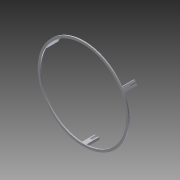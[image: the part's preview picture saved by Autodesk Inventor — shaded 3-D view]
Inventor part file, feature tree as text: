
AUTODESK INVENTOR PART (.ipt)
format: ipt  version: 2014 (Build 180170000, 170)  size: 248,832 bytes
history: native  units: mm
features: extrude x5, sketch x5
ambient origin geometry x8: Origin, YZ Plane, XZ Plane, XY Plane, X Axis, Y Axis, Z Axis, Center Point
bodies: Solid1 (feature_tree)
feature tree (10):
  extrude  "Extrusion1"  Depth=75.0mm
  extrude  "Extrusion2"  Depth=1.0mm
  extrude  "Extrusion3"  Depth=0.74mm
  extrude  "Extrusion4"  TaperAngle=45.0deg  [1 undecoded]
  extrude  "Extrusion5"  Depth=6.0mm
  sketch  "Sketch1"  dims[d0=79.0mm d1=75.0mm]
  sketch  "Sketch2"  dims[d2=1.0mm d3=0.0mm d4=1.31mm]
  sketch  "Sketch3"  dims[d5=0.74mm d6=0.76mm]
  sketch  "Sketch4"  dims[d7=0.74mm d8=45.0deg]
  sketch  "Sketch5"  dims[d9=0.75mm d10=0.523599mm d11=0.523599mm d12=1.0mm d13=30.0mm d15=360.0deg d17=11.0mm d18=0.0mm d19=6.0mm d20=0.0mm d21=6.0mm d22=0.0mm d23=6.0mm d24=0.0mm]
note: 1 required parameter value undecoded (feature->parameter linkage not recoverable at this tier; creation-order binding heuristic only, values carry confidence <= 0.55)
